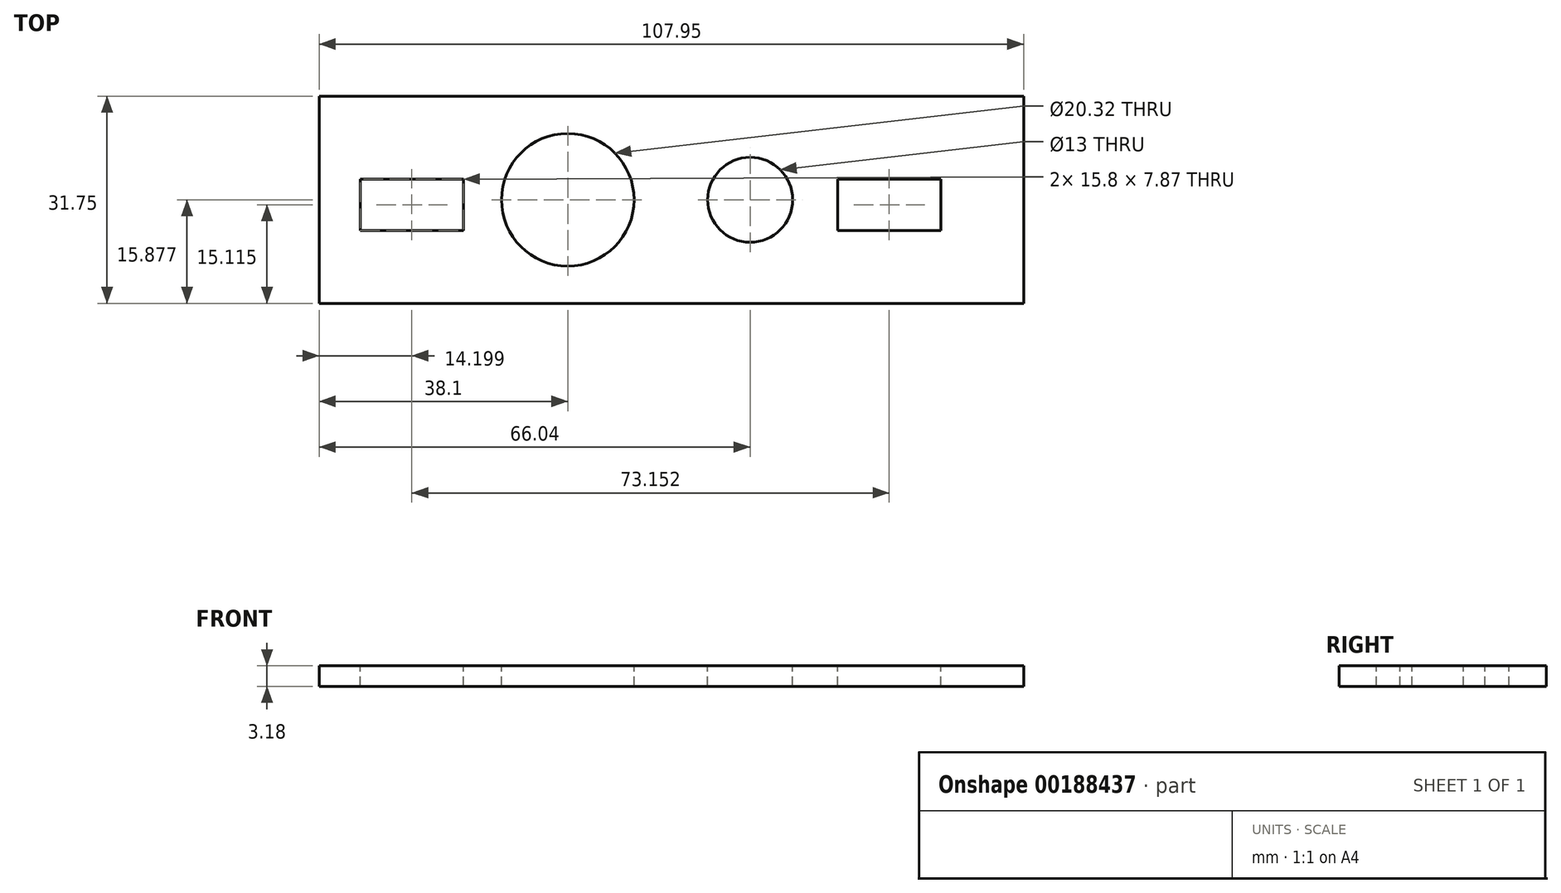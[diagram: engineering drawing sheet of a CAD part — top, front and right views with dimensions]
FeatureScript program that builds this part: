
annotation { "Feature Type Name" : "Feature", "Feature Type Description" : "" }
export const myFeature = defineFeature(function(context is Context, id is Id, definition is map)
    precondition{}
    {
        {
            var Q0;
            Q0=qCreatedBy(makeId("Top.planeOp"),FACE);
            var sketch = newSketch(context, id + "F0", { "sketchPlane" : qUnion([Q0])});
            skLineSegment(sketch, "E0.bottom", {"start": v(-66.04, 12.11) * mm, "end": v(41.9, 12.11) * mm});
            skLineSegment(sketch, "E0.top", {"start": v(-66.04, -19.64) * mm, "end": v(41.91, -19.64) * mm});
            skLineSegment(sketch, "E0.left", {"start": v(-66.04, 12.11) * mm, "end": v(-66.04, -19.64) * mm});
            skLineSegment(sketch, "E0.right", {"start": v(41.9, 12.11) * mm, "end": v(41.91, -19.64) * mm});
            skCircle(sketch, "E1", {"center": v(-27.94, -3.76) * mm, "radius": 10.16 * mm});
            skLineSegment(sketch, "E2.bottom", {"start": v(13.41, -0.59) * mm, "end": v(29.2, -0.59) * mm});
            skLineSegment(sketch, "E2.top", {"start": v(13.41, -8.46) * mm, "end": v(29.2, -8.46) * mm});
            skLineSegment(sketch, "E2.left", {"start": v(13.41, -0.59) * mm, "end": v(13.41, -8.46) * mm});
            skLineSegment(sketch, "E2.right", {"start": v(29.2, -0.59) * mm, "end": v(29.2, -8.46) * mm});
            skLineSegment(sketch, "E3.1.0.0", {"start": v(-59.74, -0.59) * mm, "end": v(-43.94, -0.59) * mm});
            skLineSegment(sketch, "E3.1.0.1", {"start": v(-59.74, -0.59) * mm, "end": v(-59.74, -8.46) * mm});
            skLineSegment(sketch, "E3.1.0.2", {"start": v(-43.94, -0.59) * mm, "end": v(-43.94, -8.46) * mm});
            skLineSegment(sketch, "E3.1.0.3", {"start": v(-59.74, -8.46) * mm, "end": v(-43.94, -8.46) * mm});
            skLineSegment(sketch, "E3.direction1", {"start": v(13.41, -0.59) * mm, "end": v(-59.74, -0.59) * mm, "construction": true});
            skCircle(sketch, "E4", {"center": v(0, -3.76) * mm, "radius": 6.5 * mm});
            skSolve(sketch);
        }
        {
            var Q0;
            Q0=makeQuery(id+"F0.imprint","IMPRINT",FACE,{"disambiguationData":[TD([[makeQuery(id+"F0.imprint","IMPRINT",EDGE,{"derivedFrom":sQuery(id+"F0.wireOp",EDGE,"E0.bottom")}),-1.0]])]});
            extrude(context, id + "F1", {"entities" : qUnion([Q0]), "oppositeDirection" : true, "depth" : 3.17 * mm});
        }
    });
